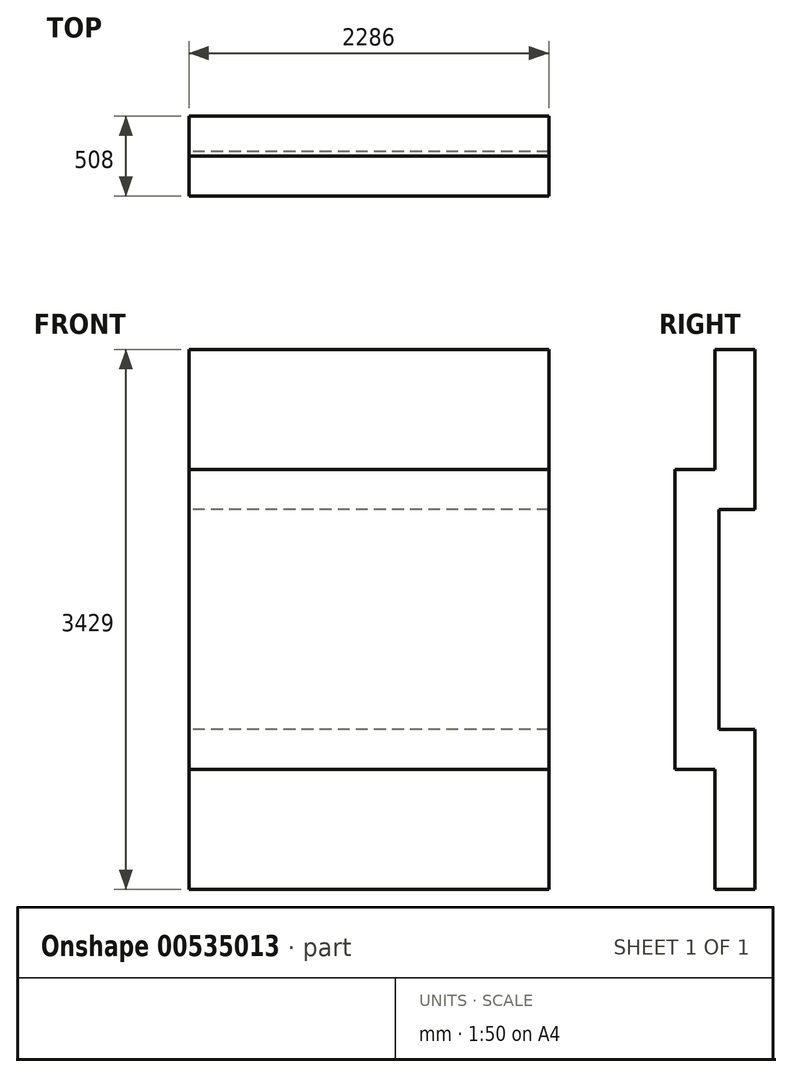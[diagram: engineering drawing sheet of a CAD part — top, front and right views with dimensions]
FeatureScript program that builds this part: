
annotation { "Feature Type Name" : "Feature", "Feature Type Description" : "" }
export const myFeature = defineFeature(function(context is Context, id is Id, definition is map)
    precondition{}
    {
        {
            var Q0;
            Q0=qCreatedBy(makeId("Right.planeOp"),FACE);
            var sketch = newSketch(context, id + "F0", { "sketchPlane" : qUnion([Q0])});
            skLineSegment(sketch, "E0.bottom", {"start": v(254, 0) * mm, "end": v(508, 0) * mm});
            skLineSegment(sketch, "E0.top", {"start": v(254, 3429) * mm, "end": v(508, 3429) * mm});
            skLineSegment(sketch, "E0.left", {"start": v(0, 762) * mm, "end": v(0, 2667) * mm});
            skLineSegment(sketch, "E0.right", {"start": v(508, 0) * mm, "end": v(508, 1016) * mm});
            skLineSegment(sketch, "E1.bottom", {"start": v(508, 1016) * mm, "end": v(281.72, 1016) * mm});
            skLineSegment(sketch, "E1.top", {"start": v(508, 2413) * mm, "end": v(281.72, 2413) * mm});
            skLineSegment(sketch, "E1.right", {"start": v(281.72, 1016) * mm, "end": v(281.72, 2413) * mm});
            skLineSegment(sketch, "E2.trimOffspring", {"start": v(508, 2413) * mm, "end": v(508, 3429) * mm});
            skLineSegment(sketch, "E3.top", {"start": v(0, 2667) * mm, "end": v(254, 2667) * mm});
            skLineSegment(sketch, "E3.right", {"start": v(254, 3429) * mm, "end": v(254, 2667) * mm});
            skLineSegment(sketch, "E4.top", {"start": v(0, 762) * mm, "end": v(254, 762) * mm});
            skLineSegment(sketch, "E4.right", {"start": v(254, 0) * mm, "end": v(254, 762) * mm});
            skSolve(sketch);
        }
        {
            var Q0;
            Q0=makeQuery(id+"F0.imprint","IMPRINT",FACE,{"disambiguationData":[TD([[makeQuery(id+"F0.imprint","IMPRINT",EDGE,{"derivedFrom":sQuery(id+"F0.wireOp",EDGE,"E0.bottom")}),1.0]])]});
            extrude(context, id + "F1", {"entities" : qUnion([Q0]), "depth" : 2286 * mm, "offsetDistance" : 25.4 * mm});
        }
    });
